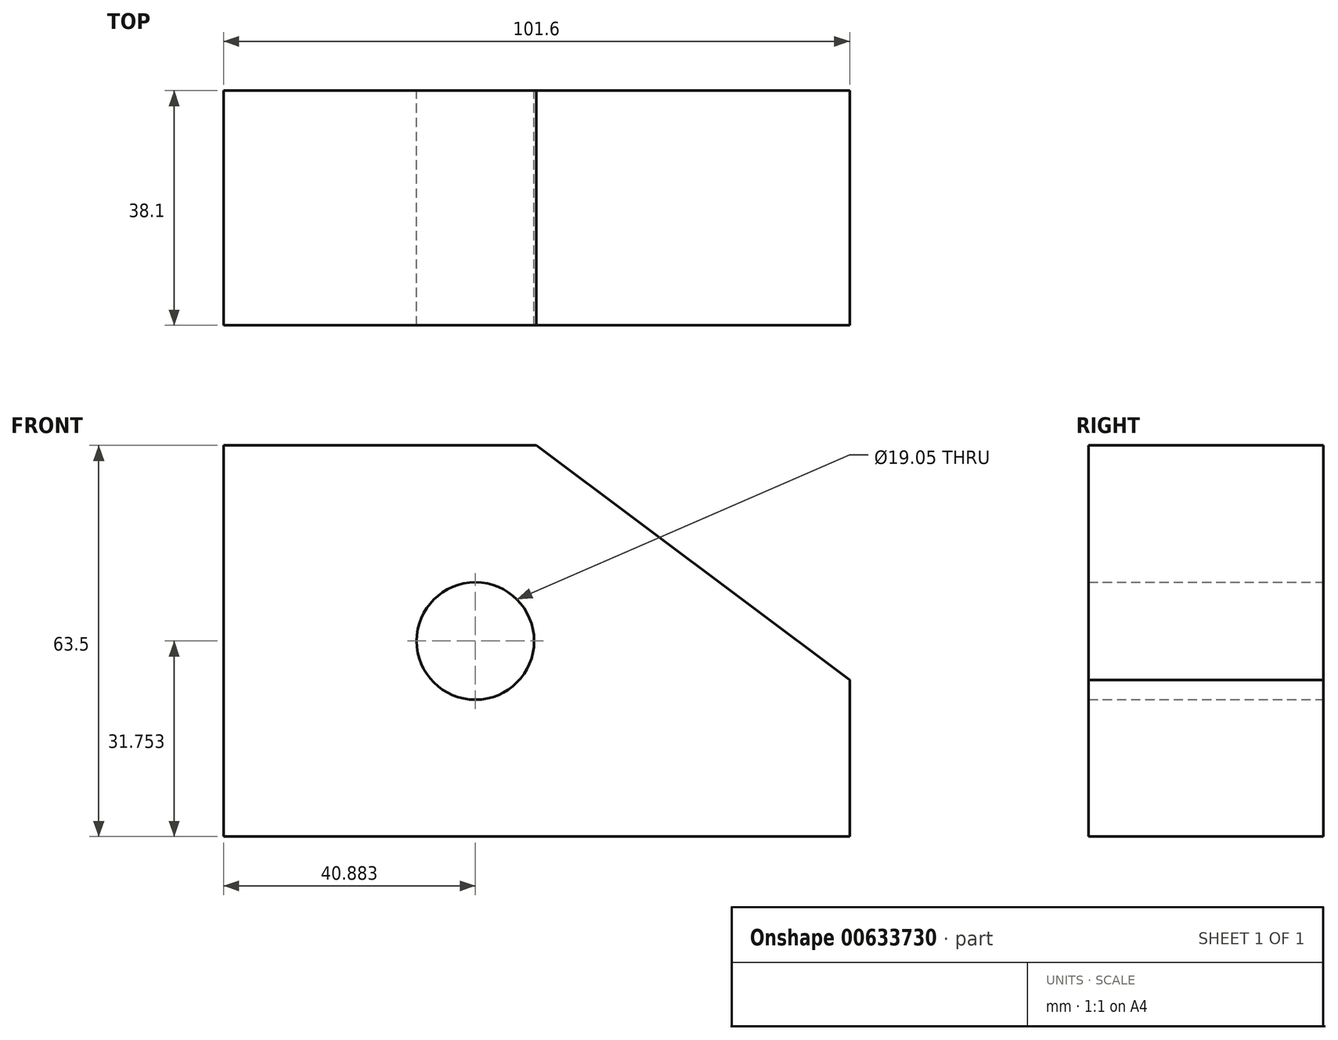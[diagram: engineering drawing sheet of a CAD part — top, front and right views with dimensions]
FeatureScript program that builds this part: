
annotation { "Feature Type Name" : "Feature", "Feature Type Description" : "" }
export const myFeature = defineFeature(function(context is Context, id is Id, definition is map)
    precondition{}
    {
        {
            var Q0;
            Q0=qCreatedBy(makeId("Front.planeOp"),FACE);
            var sketch = newSketch(context, id + "F0", { "sketchPlane" : qUnion([Q0])});
            skLineSegment(sketch, "E0", {"start": v(-76.07, 63.43) * mm, "end": v(-76.07, -0.07) * mm});
            skLineSegment(sketch, "E1", {"start": v(-76.07, -0.07) * mm, "end": v(25.53, -0.07) * mm});
            skLineSegment(sketch, "E2", {"start": v(25.53, -0.07) * mm, "end": v(25.53, 25.33) * mm});
            skLineSegment(sketch, "E3", {"start": v(-76.07, 63.43) * mm, "end": v(-25.27, 63.43) * mm});
            skLineSegment(sketch, "E4", {"start": v(-25.27, 63.43) * mm, "end": v(25.53, 25.33) * mm});
            skCircle(sketch, "E5", {"center": v(-35.19, 31.68) * mm, "radius": 9.53 * mm});
            skSolve(sketch);
        }
        {
            var Q0;
            Q0 = qSketchRegion(id + "F0", true);
            extrude(context, id + "F1", {"entities" : qUnion([Q0]), "depth" : 38.1 * mm, "offsetDistance" : 25.4 * mm});
        }
    });
